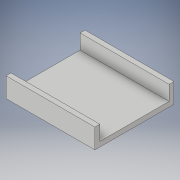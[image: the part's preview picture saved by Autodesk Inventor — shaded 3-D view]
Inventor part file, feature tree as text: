
AUTODESK INVENTOR PART (.ipt)
format: ipt  version: 2019 (Build 230136000, 136)  size: 105,984 bytes
history: native  units: in
note: dims shown in document units (in); Inventor stores cm internally (conversion verified against a paired STEP export)
features: extrude x2, sketch x1
ambient origin geometry x8: Origin, YZ Plane, XZ Plane, XY Plane, X Axis, Y Axis, Z Axis, Center Point
bodies: Solid1 (feature_tree)
feature tree (3):
  sketch  "Sketch1"  dims[d0=4.5in d1=3.5in d2=0.25in d3=0.25in d4=0.25in d5=0.0in d6=1.0in d7=0.0in]
  extrude  "Extrusion1"  Depth=3.5in
  extrude  "Extrusion2"  Depth=0.25in
